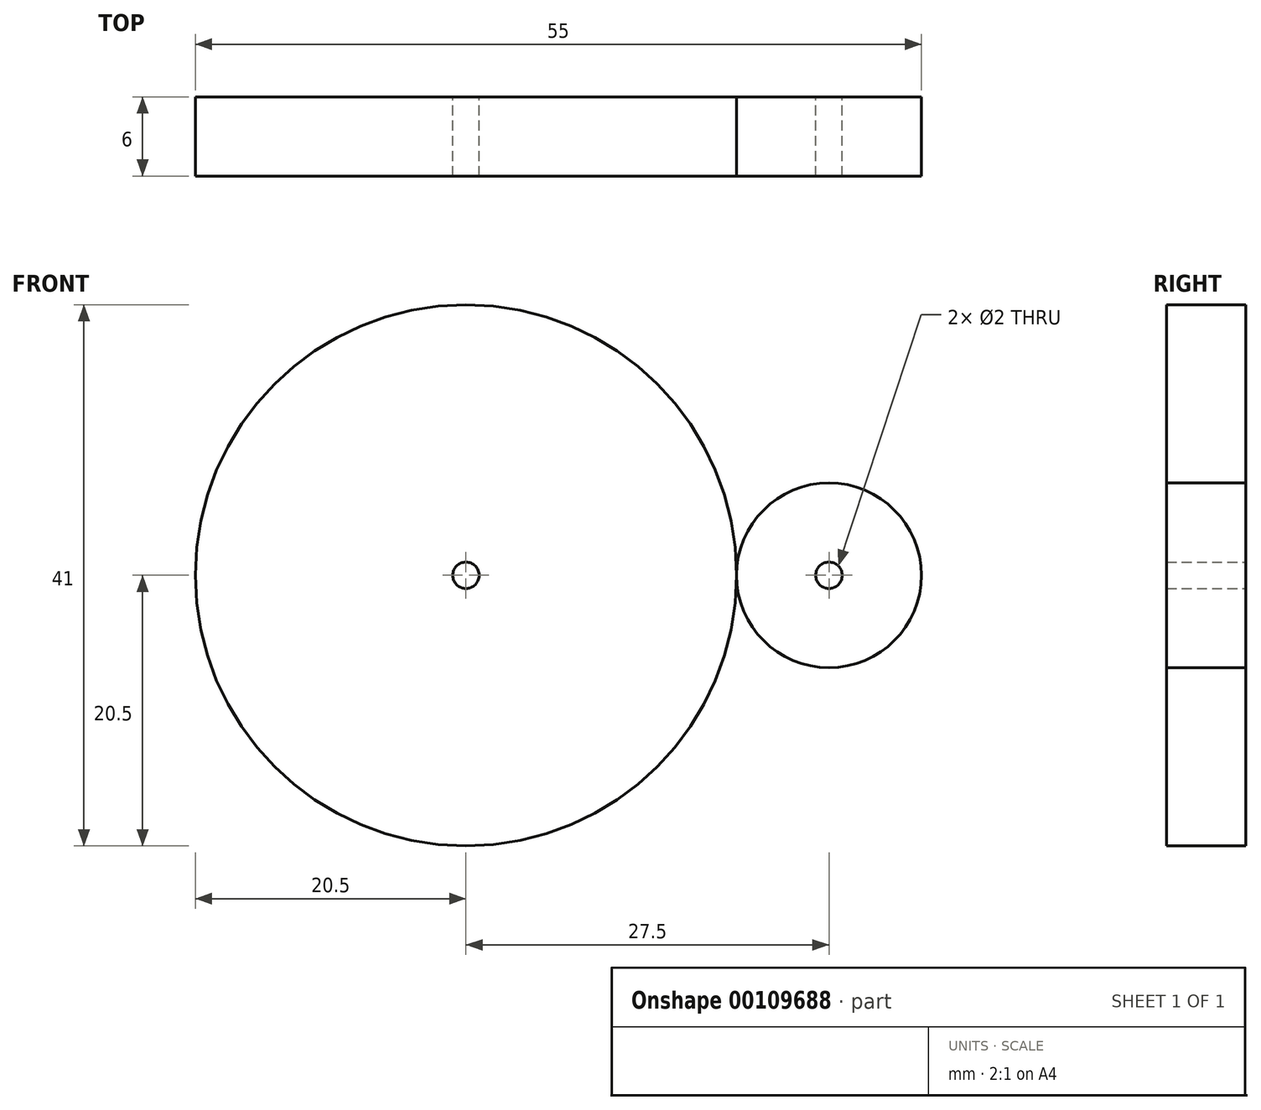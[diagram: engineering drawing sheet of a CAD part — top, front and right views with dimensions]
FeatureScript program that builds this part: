
annotation { "Feature Type Name" : "Feature", "Feature Type Description" : "" }
export const myFeature = defineFeature(function(context is Context, id is Id, definition is map)
    precondition{}
    {
        {
            var Q0;
            Q0=qCreatedBy(makeId("Front.planeOp"),FACE);
            var sketch = newSketch(context, id + "F0", { "sketchPlane" : qUnion([Q0])});
            skCircle(sketch, "E0", {"center": v(0, 0) * mm, "radius": 20.5 * mm});
            skCircle(sketch, "E1", {"center": v(27.5, 0) * mm, "radius": 7 * mm});
            skCircle(sketch, "E2", {"center": v(0, 0) * mm, "radius": 1 * mm});
            skCircle(sketch, "E3", {"center": v(27.5, 0) * mm, "radius": 1 * mm});
            skLineSegment(sketch, "E4", {"start": v(0, 0) * mm, "end": v(27.5, 0) * mm});
            skSolve(sketch);
        }
        {
            var Q0;
            Q0=makeQuery(id+"F0.imprint","IMPRINT",FACE,{"disambiguationData":[TD([[makeQuery(id+"F0.imprint","IMPRINT",EDGE,{"derivedFrom":sQuery(id+"F0.wireOp",EDGE,"E0")}),1.0]])]});
            extrude(context, id + "F1", {"entities" : qUnion([Q0]), "depth" : 6 * mm});
        }
        {
            var Q0;
            Q0=makeQuery(id+"F0.imprint","IMPRINT",FACE,{"disambiguationData":[TD([[makeQuery(id+"F0.imprint","IMPRINT",EDGE,{"derivedFrom":sQuery(id+"F0.wireOp",EDGE,"E1")}),1.0]])]});
            extrude(context, id + "F2", {"entities" : qUnion([Q0]), "operationType" : NewBodyOperationType.ADD, "depth" : 6 * mm});
        }
    });
